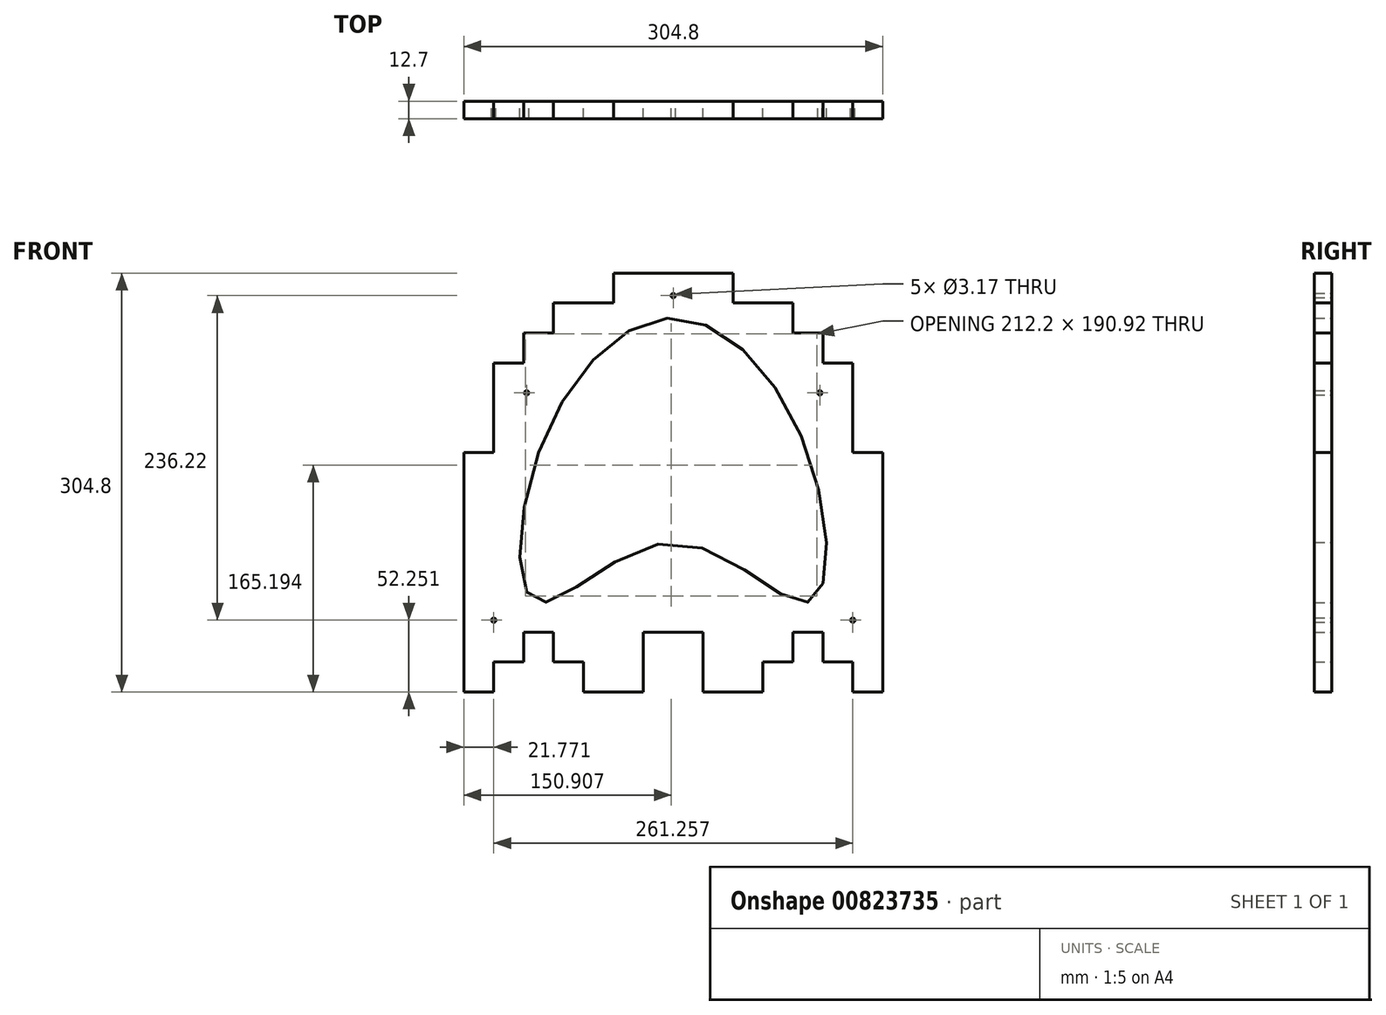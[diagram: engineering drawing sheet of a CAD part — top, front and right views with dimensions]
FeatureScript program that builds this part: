
annotation { "Feature Type Name" : "Feature", "Feature Type Description" : "" }
export const myFeature = defineFeature(function(context is Context, id is Id, definition is map)
    precondition{}
    {
        {
            var Q0;
            Q0=qCreatedBy(makeId("Front.planeOp"),FACE);
            var sketch = newSketch(context, id + "F0", { "sketchPlane" : qUnion([Q0])});
            skLineSegment(sketch, "E0", {"start": v(0, 0) * mm, "end": v(0, 174.17) * mm});
            skLineSegment(sketch, "E1", {"start": v(0, 174.17) * mm, "end": v(21.77, 174.17) * mm});
            skLineSegment(sketch, "E2", {"start": v(21.77, 174.17) * mm, "end": v(21.77, 239.49) * mm});
            skLineSegment(sketch, "E3", {"start": v(21.77, 239.49) * mm, "end": v(43.54, 239.49) * mm});
            skLineSegment(sketch, "E4", {"start": v(43.54, 239.49) * mm, "end": v(43.54, 261.26) * mm});
            skLineSegment(sketch, "E5", {"start": v(43.54, 261.26) * mm, "end": v(65.31, 261.26) * mm});
            skLineSegment(sketch, "E6", {"start": v(65.31, 261.26) * mm, "end": v(65.31, 283.03) * mm});
            skLineSegment(sketch, "E7", {"start": v(239.49, 283.03) * mm, "end": v(239.49, 261.26) * mm});
            skLineSegment(sketch, "E8", {"start": v(239.49, 261.26) * mm, "end": v(261.26, 261.26) * mm});
            skLineSegment(sketch, "E9", {"start": v(261.26, 261.26) * mm, "end": v(261.26, 239.49) * mm});
            skLineSegment(sketch, "E10", {"start": v(261.26, 239.49) * mm, "end": v(283.03, 239.49) * mm});
            skLineSegment(sketch, "E11", {"start": v(283.03, 239.49) * mm, "end": v(283.03, 174.17) * mm});
            skLineSegment(sketch, "E12", {"start": v(283.03, 174.17) * mm, "end": v(304.8, 174.17) * mm});
            skLineSegment(sketch, "E13", {"start": v(304.8, 174.17) * mm, "end": v(304.8, 0) * mm});
            skLineSegment(sketch, "E14", {"start": v(65.31, 283.03) * mm, "end": v(108.86, 283.03) * mm});
            skLineSegment(sketch, "E15", {"start": v(108.86, 283.03) * mm, "end": v(108.86, 304.8) * mm});
            skLineSegment(sketch, "E16", {"start": v(108.86, 304.8) * mm, "end": v(195.94, 304.8) * mm});
            skLineSegment(sketch, "E17", {"start": v(195.94, 304.8) * mm, "end": v(195.94, 283.03) * mm});
            skLineSegment(sketch, "E18", {"start": v(195.94, 283.03) * mm, "end": v(239.49, 283.03) * mm});
            skLineSegment(sketch, "E19", {"start": v(0, 0) * mm, "end": v(21.77, 0) * mm});
            skLineSegment(sketch, "E20", {"start": v(21.77, 0) * mm, "end": v(21.77, 21.77) * mm});
            skLineSegment(sketch, "E21", {"start": v(21.77, 21.77) * mm, "end": v(43.54, 21.77) * mm});
            skLineSegment(sketch, "E22", {"start": v(43.54, 21.77) * mm, "end": v(43.54, 43.54) * mm});
            skLineSegment(sketch, "E23", {"start": v(43.54, 43.54) * mm, "end": v(65.31, 43.54) * mm});
            skLineSegment(sketch, "E24", {"start": v(65.31, 43.54) * mm, "end": v(65.31, 21.77) * mm});
            skLineSegment(sketch, "E25", {"start": v(65.31, 21.77) * mm, "end": v(87.09, 21.77) * mm});
            skLineSegment(sketch, "E26", {"start": v(87.09, 21.77) * mm, "end": v(87.09, 0) * mm});
            skLineSegment(sketch, "E27", {"start": v(87.09, 0) * mm, "end": v(130.63, 0) * mm});
            skLineSegment(sketch, "E28", {"start": v(130.63, 0) * mm, "end": v(130.63, 43.54) * mm});
            skLineSegment(sketch, "E29", {"start": v(130.63, 43.54) * mm, "end": v(174.17, 43.54) * mm});
            skLineSegment(sketch, "E30", {"start": v(174.17, 43.54) * mm, "end": v(174.17, 0) * mm});
            skLineSegment(sketch, "E31", {"start": v(174.17, 0) * mm, "end": v(217.71, 0) * mm});
            skLineSegment(sketch, "E32", {"start": v(217.71, 0) * mm, "end": v(217.71, 21.77) * mm});
            skLineSegment(sketch, "E33", {"start": v(217.71, 21.77) * mm, "end": v(239.49, 21.77) * mm});
            skLineSegment(sketch, "E34", {"start": v(239.49, 21.77) * mm, "end": v(239.49, 43.54) * mm});
            skLineSegment(sketch, "E35", {"start": v(239.49, 43.54) * mm, "end": v(261.26, 43.54) * mm});
            skLineSegment(sketch, "E36", {"start": v(261.26, 43.54) * mm, "end": v(261.26, 21.77) * mm});
            skLineSegment(sketch, "E37", {"start": v(261.26, 21.77) * mm, "end": v(283.03, 21.77) * mm});
            skLineSegment(sketch, "E38", {"start": v(283.03, 21.77) * mm, "end": v(283.03, 0) * mm});
            skLineSegment(sketch, "E39", {"start": v(283.03, 0) * mm, "end": v(304.8, 0) * mm});
            skFitSpline(sketch, "E40", {"points": [v(54.43, 174.17) * mm, v(54.43, 65.31) * mm, v(152.4, 108.86) * mm, v(250.37, 65.31) * mm, v(250.37, 174.17) * mm, v(152.4, 272.14) * mm, v(54.43, 174.17) * mm]});
            skCircle(sketch, "E41", {"center": v(45.72, 217.71) * mm, "radius": 1.59 * mm});
            skCircle(sketch, "E42", {"center": v(259.08, 217.71) * mm, "radius": 1.59 * mm});
            skCircle(sketch, "E43", {"center": v(152.4, 288.47) * mm, "radius": 1.59 * mm});
            skCircle(sketch, "E44", {"center": v(21.77, 52.25) * mm, "radius": 1.59 * mm});
            skCircle(sketch, "E45", {"center": v(283.03, 52.25) * mm, "radius": 1.59 * mm});
            skSolve(sketch);
        }
        {
            var Q0;
            Q0=makeQuery(id+"F0.imprint","IMPRINT",FACE,{"disambiguationData":[TD([[makeQuery(id+"F0.imprint","IMPRINT",EDGE,{"derivedFrom":sQuery(id+"F0.wireOp",EDGE,"E0")}),-1.0]])]});
            extrude(context, id + "F1", {"entities" : qUnion([Q0]), "depth" : 12.7 * mm, "offsetDistance" : 25.4 * mm});
        }
    });
